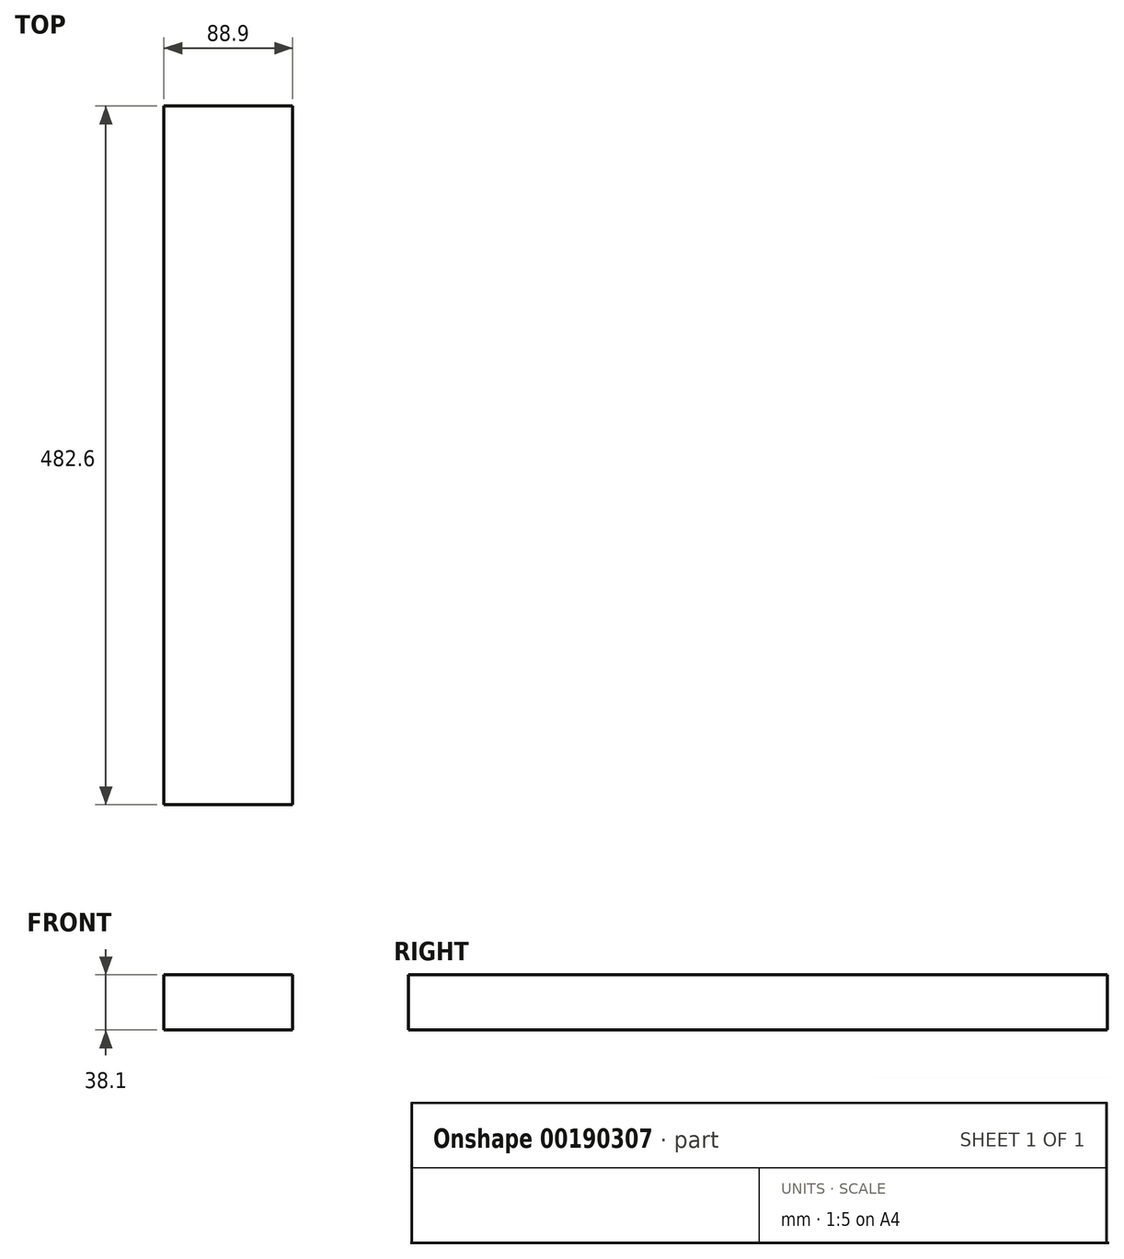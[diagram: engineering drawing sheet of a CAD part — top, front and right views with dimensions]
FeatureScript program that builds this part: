
annotation { "Feature Type Name" : "Feature", "Feature Type Description" : "" }
export const myFeature = defineFeature(function(context is Context, id is Id, definition is map)
    precondition{}
    {
        {
            var Q0;
            Q0=qCreatedBy(makeId("Front.planeOp"),FACE);
            var sketch = newSketch(context, id + "F0", { "sketchPlane" : qUnion([Q0])});
            skLineSegment(sketch, "E0.bottom", {"start": v(44.45, -19.05) * mm, "end": v(-44.45, -19.05) * mm});
            skLineSegment(sketch, "E0.top", {"start": v(44.45, 19.05) * mm, "end": v(-44.45, 19.05) * mm});
            skLineSegment(sketch, "E0.left", {"start": v(44.45, -19.05) * mm, "end": v(44.45, 19.05) * mm});
            skLineSegment(sketch, "E0.right", {"start": v(-44.45, -19.05) * mm, "end": v(-44.45, 19.05) * mm});
            skPoint(sketch, "E0.middle", {"position": v(0, 0) * mm});
            skSolve(sketch);
        }
        {
            var Q0;
            Q0=makeQuery(id+"F0.imprint","IMPRINT",FACE,{"disambiguationData":[TD([[makeQuery(id+"F0.imprint","IMPRINT",EDGE,{"derivedFrom":sQuery(id+"F0.wireOp",EDGE,"E0.bottom")}),-1.0]])]});
            extrude(context, id + "F1", {"entities" : qUnion([Q0]), "depth" : 482.6 * mm});
        }
    });
